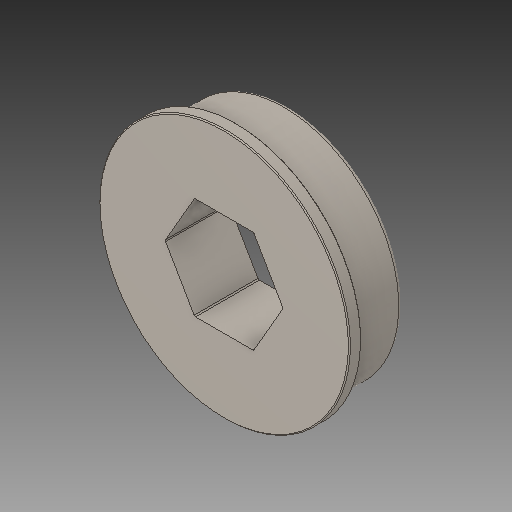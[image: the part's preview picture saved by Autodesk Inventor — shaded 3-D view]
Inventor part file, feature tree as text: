
AUTODESK INVENTOR PART (.ipt)
format: ipt  version: 2018 (Build 220112000, 112)  size: 145,408 bytes
history: native  units: in
note: dims shown in document units (in); Inventor stores cm internally (conversion verified against a paired STEP export)
features: fillet x1
ambient origin geometry x8: Origin, YZ Plane, XZ Plane, XY Plane, X Axis, Y Axis, Z Axis, Center Point
bodies: Solid1 (feature_tree)
feature tree (1):
  fillet  "Fillet2"  [1 undecoded]
note: 1 required parameter value undecoded (feature->parameter linkage not recoverable at this tier; creation-order binding heuristic only, values carry confidence <= 0.55)
